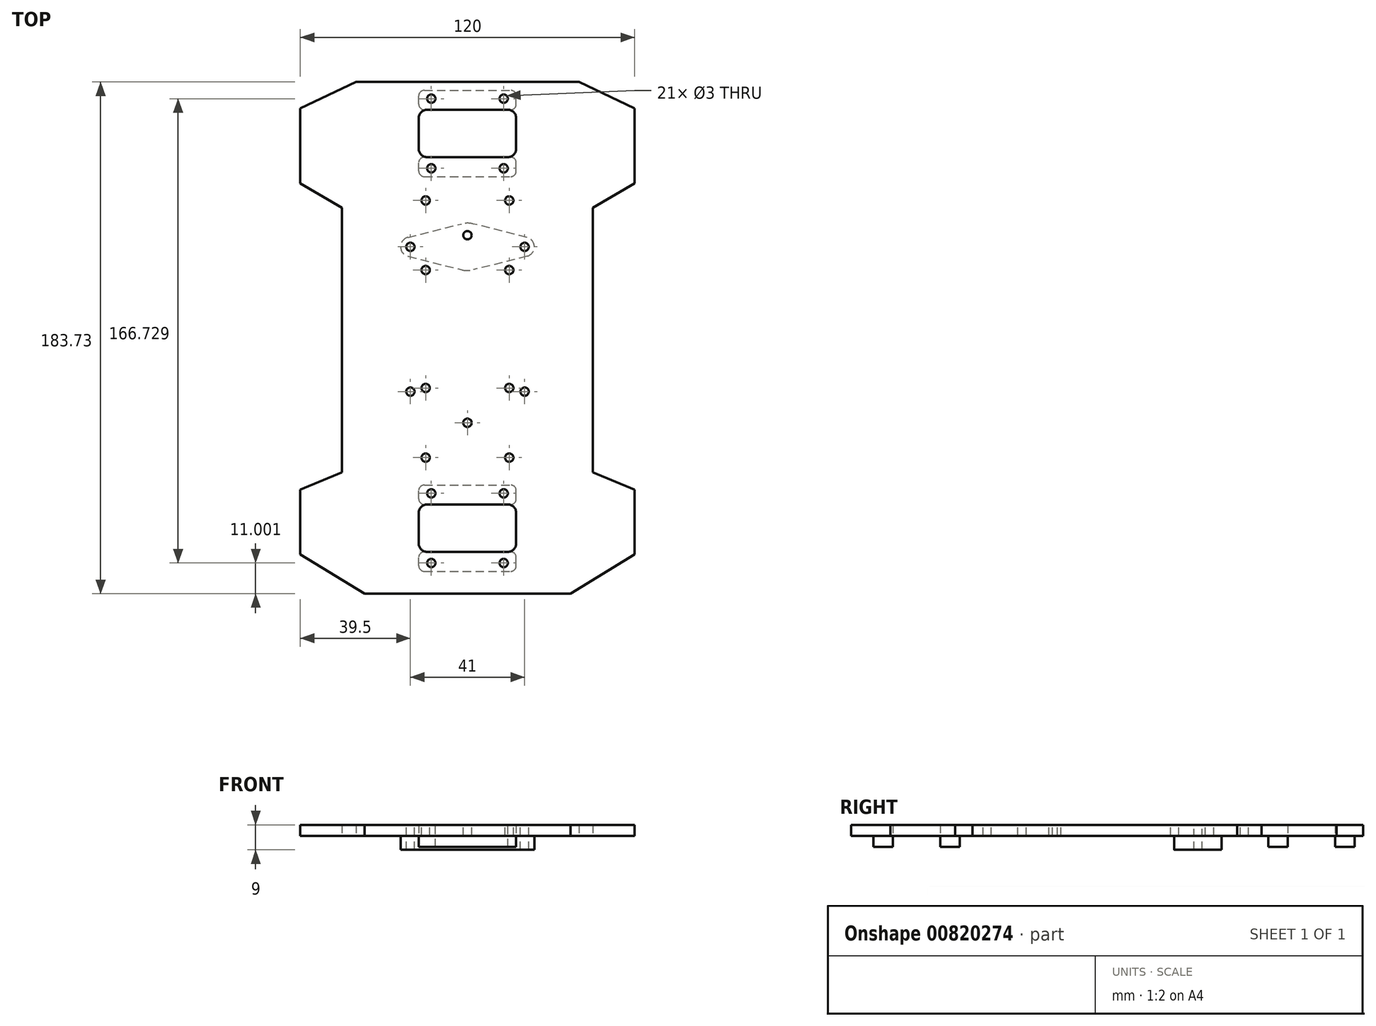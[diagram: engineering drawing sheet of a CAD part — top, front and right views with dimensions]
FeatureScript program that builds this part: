
annotation { "Feature Type Name" : "Feature", "Feature Type Description" : "" }
export const myFeature = defineFeature(function(context is Context, id is Id, definition is map)
    precondition{}
    {
        {
            var Q0;
            Q0=qCreatedBy(makeId("Top.planeOp"),FACE);
            var sketch = newSketch(context, id + "F0", { "sketchPlane" : qUnion([Q0])});
            skLineSegment(sketch, "E0", {"start": v(0, 189.63) * mm, "end": v(0, -203.58) * mm, "construction": true});
            skLineSegment(sketch, "E1", {"start": v(0, 107.51) * mm, "end": v(-40, 107.51) * mm});
            skLineSegment(sketch, "E2", {"start": v(-40, 107.51) * mm, "end": v(-60, 98) * mm});
            skLineSegment(sketch, "E3", {"start": v(-60, 98) * mm, "end": v(-60, 71.1) * mm});
            skLineSegment(sketch, "E4", {"start": v(-60, 71.1) * mm, "end": v(-45, 62.3) * mm});
            skLineSegment(sketch, "E5", {"start": v(-45, 62.3) * mm, "end": v(-45, -32.7) * mm});
            skLineSegment(sketch, "E6", {"start": v(-45, -32.7) * mm, "end": v(-60, -38.9) * mm});
            skLineSegment(sketch, "E7", {"start": v(-60, -38.9) * mm, "end": v(-60, -62.07) * mm});
            skLineSegment(sketch, "E8", {"start": v(-60, -62.07) * mm, "end": v(-36.95, -76.22) * mm});
            skLineSegment(sketch, "E9", {"start": v(-36.95, -76.22) * mm, "end": v(0, -76.22) * mm});
            skLineSegment(sketch, "E10.MirrorCS", {"start": v(45, -32.7) * mm, "end": v(60, -38.9) * mm});
            skLineSegment(sketch, "E11.MirrorCS", {"start": v(40, 107.51) * mm, "end": v(60, 98) * mm});
            skLineSegment(sketch, "E12.MirrorCS", {"start": v(60, -38.9) * mm, "end": v(60, -62.07) * mm});
            skLineSegment(sketch, "E13.MirrorCS", {"start": v(45, 62.3) * mm, "end": v(45, -32.7) * mm});
            skLineSegment(sketch, "E14.MirrorCS", {"start": v(60, -62.07) * mm, "end": v(36.95, -76.22) * mm});
            skLineSegment(sketch, "E15.MirrorCS", {"start": v(60, 71.1) * mm, "end": v(45, 62.3) * mm});
            skLineSegment(sketch, "E16.MirrorCS", {"start": v(60, 98) * mm, "end": v(60, 71.1) * mm});
            skLineSegment(sketch, "E17.MirrorCS", {"start": v(36.95, -76.22) * mm, "end": v(0, -76.22) * mm});
            skLineSegment(sketch, "E18.MirrorCS", {"start": v(0, 107.51) * mm, "end": v(40, 107.51) * mm});
            skLineSegment(sketch, "E19", {"start": v(0, -44.22) * mm, "end": v(-14.5, -44.22) * mm});
            skLineSegment(sketch, "E20", {"start": v(-17.5, -47.22) * mm, "end": v(-17.5, -58.22) * mm});
            skLineSegment(sketch, "E21", {"start": v(-14.5, -61.22) * mm, "end": v(0, -61.22) * mm});
            skLineSegment(sketch, "E22.MirrorCS", {"start": v(14.5, -61.22) * mm, "end": v(0, -61.22) * mm});
            skLineSegment(sketch, "E23.MirrorCS", {"start": v(0, -44.22) * mm, "end": v(14.5, -44.22) * mm});
            skLineSegment(sketch, "E24.MirrorCS", {"start": v(17.5, -47.22) * mm, "end": v(17.5, -58.22) * mm});
            skPoint(sketch, "E25.visualSharp", {"position": v(-17.5, -44.22) * mm});
            skArc(sketch, "E25.filletArc", {"start": v(-14.5, -44.22) * mm, "mid": v(-16.62, -45.1) * mm, "end": v(-17.5, -47.22) * mm});
            skPoint(sketch, "E26.visualSharp", {"position": v(17.5, -44.22) * mm});
            skArc(sketch, "E26.filletArc", {"start": v(17.5, -47.22) * mm, "mid": v(16.62, -45.1) * mm, "end": v(14.5, -44.22) * mm});
            skPoint(sketch, "E27.visualSharp", {"position": v(17.5, -61.22) * mm});
            skArc(sketch, "E27.filletArc", {"start": v(14.5, -61.22) * mm, "mid": v(16.62, -60.34) * mm, "end": v(17.5, -58.22) * mm});
            skPoint(sketch, "E28.visualSharp", {"position": v(-17.5, -61.22) * mm});
            skArc(sketch, "E28.filletArc", {"start": v(-17.5, -58.22) * mm, "mid": v(-16.62, -60.34) * mm, "end": v(-14.5, -61.22) * mm});
            skLineSegment(sketch, "E29", {"start": v(0, 97.51) * mm, "end": v(-14.5, 97.51) * mm});
            skLineSegment(sketch, "E30", {"start": v(-17.5, 94.51) * mm, "end": v(-17.5, 83.51) * mm});
            skLineSegment(sketch, "E31", {"start": v(-14.5, 80.51) * mm, "end": v(0, 80.51) * mm});
            skLineSegment(sketch, "E32.MirrorCS", {"start": v(14.5, 80.51) * mm, "end": v(0, 80.51) * mm});
            skLineSegment(sketch, "E33.MirrorCS", {"start": v(0, 97.51) * mm, "end": v(14.5, 97.51) * mm});
            skLineSegment(sketch, "E34.MirrorCS", {"start": v(17.5, 94.51) * mm, "end": v(17.5, 83.51) * mm});
            skPoint(sketch, "E35.visualSharp", {"position": v(-17.5, 97.51) * mm});
            skArc(sketch, "E35.filletArc", {"start": v(-14.5, 97.51) * mm, "mid": v(-16.62, 96.63) * mm, "end": v(-17.5, 94.51) * mm});
            skPoint(sketch, "E36.visualSharp", {"position": v(17.5, 97.51) * mm});
            skArc(sketch, "E36.filletArc", {"start": v(17.5, 94.51) * mm, "mid": v(16.62, 96.63) * mm, "end": v(14.5, 97.51) * mm});
            skPoint(sketch, "E37.visualSharp", {"position": v(17.5, 80.51) * mm});
            skArc(sketch, "E37.filletArc", {"start": v(14.5, 80.51) * mm, "mid": v(16.62, 81.39) * mm, "end": v(17.5, 83.51) * mm});
            skPoint(sketch, "E38.visualSharp", {"position": v(-17.5, 80.51) * mm});
            skArc(sketch, "E38.filletArc", {"start": v(-17.5, 83.51) * mm, "mid": v(-16.62, 81.39) * mm, "end": v(-14.5, 80.51) * mm});
            skSolve(sketch);
        }
        {
            var Q0;
            Q0=makeQuery(id+"F0.imprint","IMPRINT",FACE,{"disambiguationData":[TD([[makeQuery(id+"F0.imprint","IMPRINT",EDGE,{"derivedFrom":sQuery(id+"F0.wireOp",EDGE,"E1")}),1.0]])]});
            extrude(context, id + "F1", {"entities" : qUnion([Q0]), "depth" : 4 * mm, "offsetDistance" : 25 * mm});
        }
        {
            var Q0;
            Q0=makeQuery(id+"F1.opExtrude","CAP_FACE",FACE,{"disambiguationData":[OSD([sQuery(id+"F0.wireOp",EDGE,"E1"),sQuery(id+"F0.wireOp",EDGE,"E2"),sQuery(id+"F0.wireOp",EDGE,"E3"),sQuery(id+"F0.wireOp",EDGE,"E4"),sQuery(id+"F0.wireOp",EDGE,"E5"),sQuery(id+"F0.wireOp",EDGE,"E6"),sQuery(id+"F0.wireOp",EDGE,"E7"),sQuery(id+"F0.wireOp",EDGE,"E8"),sQuery(id+"F0.wireOp",EDGE,"E9"),sQuery(id+"F0.wireOp",EDGE,"E10.MirrorCS"),sQuery(id+"F0.wireOp",EDGE,"E11.MirrorCS"),sQuery(id+"F0.wireOp",EDGE,"E12.MirrorCS"),sQuery(id+"F0.wireOp",EDGE,"E13.MirrorCS"),sQuery(id+"F0.wireOp",EDGE,"E14.MirrorCS"),sQuery(id+"F0.wireOp",EDGE,"E15.MirrorCS"),sQuery(id+"F0.wireOp",EDGE,"E16.MirrorCS"),sQuery(id+"F0.wireOp",EDGE,"E17.MirrorCS"),sQuery(id+"F0.wireOp",EDGE,"E18.MirrorCS"),sQuery(id+"F0.wireOp",EDGE,"E19"),sQuery(id+"F0.wireOp",EDGE,"E20"),sQuery(id+"F0.wireOp",EDGE,"E21"),sQuery(id+"F0.wireOp",EDGE,"E22.MirrorCS"),sQuery(id+"F0.wireOp",EDGE,"E23.MirrorCS"),sQuery(id+"F0.wireOp",EDGE,"E24.MirrorCS"),sQuery(id+"F0.wireOp",EDGE,"E25.filletArc"),sQuery(id+"F0.wireOp",EDGE,"E26.filletArc"),sQuery(id+"F0.wireOp",EDGE,"E27.filletArc"),sQuery(id+"F0.wireOp",EDGE,"E28.filletArc"),sQuery(id+"F0.wireOp",EDGE,"E29"),sQuery(id+"F0.wireOp",EDGE,"E30"),sQuery(id+"F0.wireOp",EDGE,"E31"),sQuery(id+"F0.wireOp",EDGE,"E32.MirrorCS"),sQuery(id+"F0.wireOp",EDGE,"E33.MirrorCS"),sQuery(id+"F0.wireOp",EDGE,"E34.MirrorCS"),sQuery(id+"F0.wireOp",EDGE,"E35.filletArc"),sQuery(id+"F0.wireOp",EDGE,"E36.filletArc"),sQuery(id+"F0.wireOp",EDGE,"E37.filletArc"),sQuery(id+"F0.wireOp",EDGE,"E38.filletArc")])],"isStart":true});
            var sketch = newSketch(context, id + "F2", { "sketchPlane" : qUnion([Q0])});
            skLineSegment(sketch, "E39.bottom", {"start": v(-15.5, 68.22) * mm, "end": v(15.5, 68.22) * mm});
            skLineSegment(sketch, "E39.top", {"start": v(-15.5, 61.22) * mm, "end": v(15.5, 61.22) * mm});
            skLineSegment(sketch, "E39.left", {"start": v(-17.5, 66.22) * mm, "end": v(-17.5, 63.22) * mm});
            skLineSegment(sketch, "E39.right", {"start": v(17.5, 66.22) * mm, "end": v(17.5, 63.22) * mm});
            skLineSegment(sketch, "E40.bottom", {"start": v(-15.5, 44.22) * mm, "end": v(15.5, 44.22) * mm});
            skLineSegment(sketch, "E40.top", {"start": v(-15.5, 37.22) * mm, "end": v(15.5, 37.22) * mm});
            skLineSegment(sketch, "E40.left", {"start": v(-17.5, 42.22) * mm, "end": v(-17.5, 39.22) * mm});
            skLineSegment(sketch, "E40.right", {"start": v(17.5, 42.22) * mm, "end": v(17.5, 39.22) * mm});
            skLineSegment(sketch, "E41.bottom", {"start": v(-15.5, -73.51) * mm, "end": v(15.5, -73.51) * mm});
            skLineSegment(sketch, "E41.top", {"start": v(-15.5, -80.51) * mm, "end": v(15.5, -80.51) * mm});
            skLineSegment(sketch, "E41.left", {"start": v(-17.5, -75.51) * mm, "end": v(-17.5, -78.51) * mm});
            skLineSegment(sketch, "E41.right", {"start": v(17.5, -75.51) * mm, "end": v(17.5, -78.51) * mm});
            skLineSegment(sketch, "E42.bottom", {"start": v(-15.5, -97.51) * mm, "end": v(15.5, -97.51) * mm});
            skLineSegment(sketch, "E42.top", {"start": v(-15.5, -104.51) * mm, "end": v(15.5, -104.51) * mm});
            skLineSegment(sketch, "E42.left", {"start": v(-17.5, -99.51) * mm, "end": v(-17.5, -102.51) * mm});
            skLineSegment(sketch, "E42.right", {"start": v(17.5, -99.51) * mm, "end": v(17.5, -102.51) * mm});
            skPoint(sketch, "E43.visualSharp", {"position": v(-17.5, -73.51) * mm});
            skArc(sketch, "E43.filletArc", {"start": v(-15.5, -73.51) * mm, "mid": v(-16.91, -74.1) * mm, "end": v(-17.5, -75.51) * mm});
            skPoint(sketch, "E44.visualSharp", {"position": v(-17.5, -80.51) * mm});
            skArc(sketch, "E44.filletArc", {"start": v(-17.5, -78.51) * mm, "mid": v(-16.91, -79.92) * mm, "end": v(-15.5, -80.51) * mm});
            skPoint(sketch, "E45.visualSharp", {"position": v(17.5, -80.51) * mm});
            skArc(sketch, "E45.filletArc", {"start": v(15.5, -80.51) * mm, "mid": v(16.91, -79.92) * mm, "end": v(17.5, -78.51) * mm});
            skPoint(sketch, "E46.visualSharp", {"position": v(17.5, -73.51) * mm});
            skArc(sketch, "E46.filletArc", {"start": v(17.5, -75.51) * mm, "mid": v(16.91, -74.1) * mm, "end": v(15.5, -73.51) * mm});
            skPoint(sketch, "E47.visualSharp", {"position": v(17.5, -97.51) * mm});
            skArc(sketch, "E47.filletArc", {"start": v(17.5, -99.51) * mm, "mid": v(16.91, -98.1) * mm, "end": v(15.5, -97.51) * mm});
            skPoint(sketch, "E48.visualSharp", {"position": v(17.5, -104.51) * mm});
            skArc(sketch, "E48.filletArc", {"start": v(15.5, -104.51) * mm, "mid": v(16.91, -103.92) * mm, "end": v(17.5, -102.51) * mm});
            skPoint(sketch, "E49.visualSharp", {"position": v(-17.5, -104.51) * mm});
            skArc(sketch, "E49.filletArc", {"start": v(-17.5, -102.51) * mm, "mid": v(-16.91, -103.92) * mm, "end": v(-15.5, -104.51) * mm});
            skPoint(sketch, "E50.visualSharp", {"position": v(-17.5, -97.51) * mm});
            skArc(sketch, "E50.filletArc", {"start": v(-15.5, -97.51) * mm, "mid": v(-16.91, -98.1) * mm, "end": v(-17.5, -99.51) * mm});
            skPoint(sketch, "E51.visualSharp", {"position": v(-17.5, 37.22) * mm});
            skArc(sketch, "E51.filletArc", {"start": v(-17.5, 39.22) * mm, "mid": v(-16.91, 37.8) * mm, "end": v(-15.5, 37.22) * mm});
            skPoint(sketch, "E52.visualSharp", {"position": v(-17.5, 44.22) * mm});
            skArc(sketch, "E52.filletArc", {"start": v(-15.5, 44.22) * mm, "mid": v(-16.91, 43.63) * mm, "end": v(-17.5, 42.22) * mm});
            skPoint(sketch, "E53.visualSharp", {"position": v(17.5, 37.22) * mm});
            skArc(sketch, "E53.filletArc", {"start": v(15.5, 37.22) * mm, "mid": v(16.91, 37.8) * mm, "end": v(17.5, 39.22) * mm});
            skPoint(sketch, "E54.visualSharp", {"position": v(17.5, 61.22) * mm});
            skArc(sketch, "E54.filletArc", {"start": v(15.5, 61.22) * mm, "mid": v(16.91, 61.8) * mm, "end": v(17.5, 63.22) * mm});
            skPoint(sketch, "E55.visualSharp", {"position": v(17.5, 68.22) * mm});
            skArc(sketch, "E55.filletArc", {"start": v(17.5, 66.22) * mm, "mid": v(16.91, 67.63) * mm, "end": v(15.5, 68.22) * mm});
            skPoint(sketch, "E56.visualSharp", {"position": v(-17.5, 68.22) * mm});
            skArc(sketch, "E56.filletArc", {"start": v(-15.5, 68.22) * mm, "mid": v(-16.91, 67.63) * mm, "end": v(-17.5, 66.22) * mm});
            skPoint(sketch, "E57.visualSharp", {"position": v(-17.5, 61.22) * mm});
            skArc(sketch, "E57.filletArc", {"start": v(-17.5, 63.22) * mm, "mid": v(-16.91, 61.8) * mm, "end": v(-15.5, 61.22) * mm});
            skPoint(sketch, "E58.visualSharp", {"position": v(17.5, 44.22) * mm});
            skArc(sketch, "E58.filletArc", {"start": v(17.5, 42.22) * mm, "mid": v(16.91, 43.63) * mm, "end": v(15.5, 44.22) * mm});
            skSolve(sketch);
        }
        {
            var Q0;
            Q0 = qSketchRegion(id + "F2", true);
            extrude(context, id + "F3", {"entities" : qUnion([Q0]), "operationType" : NewBodyOperationType.ADD, "depth" : 4 * mm, "offsetDistance" : 25 * mm});
        }
        {
            var Q0;
            Q0=makeQuery(id+"F1.opExtrude","CAP_FACE",FACE,{"disambiguationData":[OSD([sQuery(id+"F0.wireOp",EDGE,"E1"),sQuery(id+"F0.wireOp",EDGE,"E2"),sQuery(id+"F0.wireOp",EDGE,"E3"),sQuery(id+"F0.wireOp",EDGE,"E4"),sQuery(id+"F0.wireOp",EDGE,"E5"),sQuery(id+"F0.wireOp",EDGE,"E6"),sQuery(id+"F0.wireOp",EDGE,"E7"),sQuery(id+"F0.wireOp",EDGE,"E8"),sQuery(id+"F0.wireOp",EDGE,"E9"),sQuery(id+"F0.wireOp",EDGE,"E10.MirrorCS"),sQuery(id+"F0.wireOp",EDGE,"E11.MirrorCS"),sQuery(id+"F0.wireOp",EDGE,"E12.MirrorCS"),sQuery(id+"F0.wireOp",EDGE,"E13.MirrorCS"),sQuery(id+"F0.wireOp",EDGE,"E14.MirrorCS"),sQuery(id+"F0.wireOp",EDGE,"E15.MirrorCS"),sQuery(id+"F0.wireOp",EDGE,"E16.MirrorCS"),sQuery(id+"F0.wireOp",EDGE,"E17.MirrorCS"),sQuery(id+"F0.wireOp",EDGE,"E18.MirrorCS"),sQuery(id+"F0.wireOp",EDGE,"E19"),sQuery(id+"F0.wireOp",EDGE,"E20"),sQuery(id+"F0.wireOp",EDGE,"E21"),sQuery(id+"F0.wireOp",EDGE,"E22.MirrorCS"),sQuery(id+"F0.wireOp",EDGE,"E23.MirrorCS"),sQuery(id+"F0.wireOp",EDGE,"E24.MirrorCS"),sQuery(id+"F0.wireOp",EDGE,"E25.filletArc"),sQuery(id+"F0.wireOp",EDGE,"E26.filletArc"),sQuery(id+"F0.wireOp",EDGE,"E27.filletArc"),sQuery(id+"F0.wireOp",EDGE,"E28.filletArc"),sQuery(id+"F0.wireOp",EDGE,"E29"),sQuery(id+"F0.wireOp",EDGE,"E30"),sQuery(id+"F0.wireOp",EDGE,"E31"),sQuery(id+"F0.wireOp",EDGE,"E32.MirrorCS"),sQuery(id+"F0.wireOp",EDGE,"E33.MirrorCS"),sQuery(id+"F0.wireOp",EDGE,"E34.MirrorCS"),sQuery(id+"F0.wireOp",EDGE,"E35.filletArc"),sQuery(id+"F0.wireOp",EDGE,"E36.filletArc"),sQuery(id+"F0.wireOp",EDGE,"E37.filletArc"),sQuery(id+"F0.wireOp",EDGE,"E38.filletArc")])],"isStart":false});
            var sketch = newSketch(context, id + "F4", { "sketchPlane" : qUnion([Q0])});
            skCircle(sketch, "E59", {"center": v(-20.5, 48.3) * mm, "radius": 1.5 * mm});
            skCircle(sketch, "E60.0.1.0", {"center": v(-20.5, -3.7) * mm, "radius": 1.5 * mm});
            skCircle(sketch, "E60.1.0.0", {"center": v(20.5, 48.3) * mm, "radius": 1.5 * mm});
            skCircle(sketch, "E60.1.1.0", {"center": v(20.5, -3.7) * mm, "radius": 1.5 * mm});
            skLineSegment(sketch, "E60.direction1", {"start": v(-20.5, 48.3) * mm, "end": v(20.5, 48.3) * mm, "construction": true});
            skLineSegment(sketch, "E60.direction2", {"start": v(-20.5, 48.3) * mm, "end": v(-20.5, -3.7) * mm, "construction": true});
            skLineSegment(sketch, "E61", {"start": v(0, 70.67) * mm, "end": v(0, -11.9) * mm, "construction": true});
            skLineSegment(sketch, "E62", {"start": v(-45, 62.3) * mm, "end": v(45, 62.3) * mm, "construction": true});
            skSolve(sketch);
        }
        {
            var Q0;
            Q0 = qSketchRegion(id + "F4", true);
            extrude(context, id + "F5", {"entities" : qUnion([Q0]), "operationType" : NewBodyOperationType.REMOVE, "oppositeDirection" : true, "depth" : 25 * mm, "offsetDistance" : 25 * mm});
        }
        {
            var Q0;
            Q0=makeQuery(id+"F1.opExtrude","CAP_FACE",FACE,{"disambiguationData":[OSD([sQuery(id+"F0.wireOp",EDGE,"E1"),sQuery(id+"F0.wireOp",EDGE,"E2"),sQuery(id+"F0.wireOp",EDGE,"E3"),sQuery(id+"F0.wireOp",EDGE,"E4"),sQuery(id+"F0.wireOp",EDGE,"E5"),sQuery(id+"F0.wireOp",EDGE,"E6"),sQuery(id+"F0.wireOp",EDGE,"E7"),sQuery(id+"F0.wireOp",EDGE,"E8"),sQuery(id+"F0.wireOp",EDGE,"E9"),sQuery(id+"F0.wireOp",EDGE,"E10.MirrorCS"),sQuery(id+"F0.wireOp",EDGE,"E11.MirrorCS"),sQuery(id+"F0.wireOp",EDGE,"E12.MirrorCS"),sQuery(id+"F0.wireOp",EDGE,"E13.MirrorCS"),sQuery(id+"F0.wireOp",EDGE,"E14.MirrorCS"),sQuery(id+"F0.wireOp",EDGE,"E15.MirrorCS"),sQuery(id+"F0.wireOp",EDGE,"E16.MirrorCS"),sQuery(id+"F0.wireOp",EDGE,"E17.MirrorCS"),sQuery(id+"F0.wireOp",EDGE,"E18.MirrorCS"),sQuery(id+"F0.wireOp",EDGE,"E19"),sQuery(id+"F0.wireOp",EDGE,"E20"),sQuery(id+"F0.wireOp",EDGE,"E21"),sQuery(id+"F0.wireOp",EDGE,"E22.MirrorCS"),sQuery(id+"F0.wireOp",EDGE,"E23.MirrorCS"),sQuery(id+"F0.wireOp",EDGE,"E24.MirrorCS"),sQuery(id+"F0.wireOp",EDGE,"E25.filletArc"),sQuery(id+"F0.wireOp",EDGE,"E26.filletArc"),sQuery(id+"F0.wireOp",EDGE,"E27.filletArc"),sQuery(id+"F0.wireOp",EDGE,"E28.filletArc"),sQuery(id+"F0.wireOp",EDGE,"E29"),sQuery(id+"F0.wireOp",EDGE,"E30"),sQuery(id+"F0.wireOp",EDGE,"E31"),sQuery(id+"F0.wireOp",EDGE,"E32.MirrorCS"),sQuery(id+"F0.wireOp",EDGE,"E33.MirrorCS"),sQuery(id+"F0.wireOp",EDGE,"E34.MirrorCS"),sQuery(id+"F0.wireOp",EDGE,"E35.filletArc"),sQuery(id+"F0.wireOp",EDGE,"E36.filletArc"),sQuery(id+"F0.wireOp",EDGE,"E37.filletArc"),sQuery(id+"F0.wireOp",EDGE,"E38.filletArc")])],"isStart":false});
            var sketch = newSketch(context, id + "F6", { "sketchPlane" : qUnion([Q0])});
            skCircle(sketch, "E63", {"center": v(-13, -40.22) * mm, "radius": 1.5 * mm});
            skCircle(sketch, "E64.0.1.0", {"center": v(-13, -65.22) * mm, "radius": 1.5 * mm});
            skCircle(sketch, "E64.1.0.0", {"center": v(13, -40.22) * mm, "radius": 1.5 * mm});
            skCircle(sketch, "E64.1.1.0", {"center": v(13, -65.22) * mm, "radius": 1.5 * mm});
            skLineSegment(sketch, "E64.direction1", {"start": v(-13, -40.22) * mm, "end": v(13, -40.22) * mm, "construction": true});
            skLineSegment(sketch, "E64.direction2", {"start": v(-13, -40.22) * mm, "end": v(-13, -65.22) * mm, "construction": true});
            skLineSegment(sketch, "E65", {"start": v(13, -65.22) * mm, "end": v(-13, -65.22) * mm, "construction": true});
            skLineSegment(sketch, "E66", {"start": v(-17.5, -52.72) * mm, "end": v(17.5, -52.72) * mm, "construction": true});
            skLineSegment(sketch, "E67", {"start": v(0, -44.22) * mm, "end": v(0, -61.22) * mm, "construction": true});
            skCircle(sketch, "E68", {"center": v(-13, 101.51) * mm, "radius": 1.5 * mm});
            skCircle(sketch, "E69.0.1.0", {"center": v(-13, 76.51) * mm, "radius": 1.5 * mm});
            skCircle(sketch, "E69.1.0.0", {"center": v(13, 101.51) * mm, "radius": 1.5 * mm});
            skCircle(sketch, "E69.1.1.0", {"center": v(13, 76.51) * mm, "radius": 1.5 * mm});
            skLineSegment(sketch, "E69.direction1", {"start": v(-13, 101.51) * mm, "end": v(13, 101.51) * mm, "construction": true});
            skLineSegment(sketch, "E69.direction2", {"start": v(-13, 101.51) * mm, "end": v(-13, 76.51) * mm, "construction": true});
            skLineSegment(sketch, "E70", {"start": v(13, 76.51) * mm, "end": v(-13, 76.51) * mm, "construction": true});
            skLineSegment(sketch, "E71", {"start": v(0, 106.76) * mm, "end": v(0, 57.44) * mm, "construction": true});
            skLineSegment(sketch, "E72", {"start": v(-17.5, 89.01) * mm, "end": v(17.5, 89.01) * mm, "construction": true});
            skSolve(sketch);
        }
        {
            var Q0;
            Q0 = qSketchRegion(id + "F6", true);
            extrude(context, id + "F7", {"entities" : qUnion([Q0]), "operationType" : NewBodyOperationType.REMOVE, "oppositeDirection" : true, "depth" : 25 * mm, "offsetDistance" : 25 * mm});
        }
        {
            var Q0;
            Q0=makeQuery(id+"F1.opExtrude","CAP_FACE",FACE,{"disambiguationData":[OSD([sQuery(id+"F0.wireOp",EDGE,"E1"),sQuery(id+"F0.wireOp",EDGE,"E2"),sQuery(id+"F0.wireOp",EDGE,"E3"),sQuery(id+"F0.wireOp",EDGE,"E4"),sQuery(id+"F0.wireOp",EDGE,"E5"),sQuery(id+"F0.wireOp",EDGE,"E6"),sQuery(id+"F0.wireOp",EDGE,"E7"),sQuery(id+"F0.wireOp",EDGE,"E8"),sQuery(id+"F0.wireOp",EDGE,"E9"),sQuery(id+"F0.wireOp",EDGE,"E10.MirrorCS"),sQuery(id+"F0.wireOp",EDGE,"E11.MirrorCS"),sQuery(id+"F0.wireOp",EDGE,"E12.MirrorCS"),sQuery(id+"F0.wireOp",EDGE,"E13.MirrorCS"),sQuery(id+"F0.wireOp",EDGE,"E14.MirrorCS"),sQuery(id+"F0.wireOp",EDGE,"E15.MirrorCS"),sQuery(id+"F0.wireOp",EDGE,"E16.MirrorCS"),sQuery(id+"F0.wireOp",EDGE,"E17.MirrorCS"),sQuery(id+"F0.wireOp",EDGE,"E18.MirrorCS"),sQuery(id+"F0.wireOp",EDGE,"E19"),sQuery(id+"F0.wireOp",EDGE,"E20"),sQuery(id+"F0.wireOp",EDGE,"E21"),sQuery(id+"F0.wireOp",EDGE,"E22.MirrorCS"),sQuery(id+"F0.wireOp",EDGE,"E23.MirrorCS"),sQuery(id+"F0.wireOp",EDGE,"E24.MirrorCS"),sQuery(id+"F0.wireOp",EDGE,"E25.filletArc"),sQuery(id+"F0.wireOp",EDGE,"E26.filletArc"),sQuery(id+"F0.wireOp",EDGE,"E27.filletArc"),sQuery(id+"F0.wireOp",EDGE,"E28.filletArc"),sQuery(id+"F0.wireOp",EDGE,"E29"),sQuery(id+"F0.wireOp",EDGE,"E30"),sQuery(id+"F0.wireOp",EDGE,"E31"),sQuery(id+"F0.wireOp",EDGE,"E32.MirrorCS"),sQuery(id+"F0.wireOp",EDGE,"E33.MirrorCS"),sQuery(id+"F0.wireOp",EDGE,"E34.MirrorCS"),sQuery(id+"F0.wireOp",EDGE,"E35.filletArc"),sQuery(id+"F0.wireOp",EDGE,"E36.filletArc"),sQuery(id+"F0.wireOp",EDGE,"E37.filletArc"),sQuery(id+"F0.wireOp",EDGE,"E38.filletArc")])],"isStart":false});
            var sketch = newSketch(context, id + "F8", { "sketchPlane" : qUnion([Q0])});
            skCircle(sketch, "E73", {"center": v(-15, -2.38) * mm, "radius": 1.5 * mm});
            skCircle(sketch, "E74.0.1.0", {"center": v(-15, -27.38) * mm, "radius": 1.5 * mm});
            skCircle(sketch, "E74.1.0.0", {"center": v(15, -2.38) * mm, "radius": 1.5 * mm});
            skCircle(sketch, "E74.1.1.0", {"center": v(15, -27.38) * mm, "radius": 1.5 * mm});
            skLineSegment(sketch, "E74.direction1", {"start": v(-15, -2.38) * mm, "end": v(15, -2.38) * mm, "construction": true});
            skLineSegment(sketch, "E74.direction2", {"start": v(-15, -2.38) * mm, "end": v(-15, -27.38) * mm, "construction": true});
            skLineSegment(sketch, "E75", {"start": v(0, 0) * mm, "end": v(0, -52.65) * mm, "construction": true});
            skCircle(sketch, "E76", {"center": v(-15, 64.97) * mm, "radius": 1.5 * mm});
            skCircle(sketch, "E77.0.1.0", {"center": v(-15, 39.97) * mm, "radius": 1.5 * mm});
            skCircle(sketch, "E77.1.0.0", {"center": v(15, 64.97) * mm, "radius": 1.5 * mm});
            skCircle(sketch, "E77.1.1.0", {"center": v(15, 39.97) * mm, "radius": 1.5 * mm});
            skLineSegment(sketch, "E77.direction1", {"start": v(-15, 64.97) * mm, "end": v(15, 64.97) * mm, "construction": true});
            skLineSegment(sketch, "E77.direction2", {"start": v(-15, 64.97) * mm, "end": v(-15, 39.97) * mm, "construction": true});
            skLineSegment(sketch, "E78", {"start": v(15, -27.38) * mm, "end": v(-15, -2.38) * mm, "construction": true});
            skLineSegment(sketch, "E79", {"start": v(15, -2.38) * mm, "end": v(-15, -27.38) * mm, "construction": true});
            skLineSegment(sketch, "E80", {"start": v(15, 39.97) * mm, "end": v(-15, 64.97) * mm, "construction": true});
            skLineSegment(sketch, "E81", {"start": v(15, 64.97) * mm, "end": v(-15, 39.97) * mm, "construction": true});
            skCircle(sketch, "E82", {"center": v(0, 52.47) * mm, "radius": 1.5 * mm});
            skCircle(sketch, "E83", {"center": v(0, -14.88) * mm, "radius": 1.5 * mm});
            skSolve(sketch);
        }
        {
            var Q0;
            Q0 = qSketchRegion(id + "F8", true);
            extrude(context, id + "F9", {"entities" : qUnion([Q0]), "operationType" : NewBodyOperationType.REMOVE, "oppositeDirection" : true, "depth" : 25 * mm, "offsetDistance" : 25 * mm});
        }
        {
            var Q0;
            Q0=makeQuery(id+"F1.opExtrude","CAP_FACE",FACE,{"disambiguationData":[OSD([sQuery(id+"F0.wireOp",EDGE,"E1"),sQuery(id+"F0.wireOp",EDGE,"E2"),sQuery(id+"F0.wireOp",EDGE,"E3"),sQuery(id+"F0.wireOp",EDGE,"E4"),sQuery(id+"F0.wireOp",EDGE,"E5"),sQuery(id+"F0.wireOp",EDGE,"E6"),sQuery(id+"F0.wireOp",EDGE,"E7"),sQuery(id+"F0.wireOp",EDGE,"E8"),sQuery(id+"F0.wireOp",EDGE,"E9"),sQuery(id+"F0.wireOp",EDGE,"E10.MirrorCS"),sQuery(id+"F0.wireOp",EDGE,"E11.MirrorCS"),sQuery(id+"F0.wireOp",EDGE,"E12.MirrorCS"),sQuery(id+"F0.wireOp",EDGE,"E13.MirrorCS"),sQuery(id+"F0.wireOp",EDGE,"E14.MirrorCS"),sQuery(id+"F0.wireOp",EDGE,"E15.MirrorCS"),sQuery(id+"F0.wireOp",EDGE,"E16.MirrorCS"),sQuery(id+"F0.wireOp",EDGE,"E17.MirrorCS"),sQuery(id+"F0.wireOp",EDGE,"E18.MirrorCS"),sQuery(id+"F0.wireOp",EDGE,"E19"),sQuery(id+"F0.wireOp",EDGE,"E20"),sQuery(id+"F0.wireOp",EDGE,"E21"),sQuery(id+"F0.wireOp",EDGE,"E22.MirrorCS"),sQuery(id+"F0.wireOp",EDGE,"E23.MirrorCS"),sQuery(id+"F0.wireOp",EDGE,"E24.MirrorCS"),sQuery(id+"F0.wireOp",EDGE,"E25.filletArc"),sQuery(id+"F0.wireOp",EDGE,"E26.filletArc"),sQuery(id+"F0.wireOp",EDGE,"E27.filletArc"),sQuery(id+"F0.wireOp",EDGE,"E28.filletArc"),sQuery(id+"F0.wireOp",EDGE,"E29"),sQuery(id+"F0.wireOp",EDGE,"E30"),sQuery(id+"F0.wireOp",EDGE,"E31"),sQuery(id+"F0.wireOp",EDGE,"E32.MirrorCS"),sQuery(id+"F0.wireOp",EDGE,"E33.MirrorCS"),sQuery(id+"F0.wireOp",EDGE,"E34.MirrorCS"),sQuery(id+"F0.wireOp",EDGE,"E35.filletArc"),sQuery(id+"F0.wireOp",EDGE,"E36.filletArc"),sQuery(id+"F0.wireOp",EDGE,"E37.filletArc"),sQuery(id+"F0.wireOp",EDGE,"E38.filletArc")])],"isStart":true});
            var sketch = newSketch(context, id + "F10", { "sketchPlane" : qUnion([Q0])});
            skLineSegment(sketch, "E84", {"start": v(20.5, -48.3) * mm, "end": v(-20.5, -48.3) * mm, "construction": true});
            skArc(sketch, "E85", {"start": v(2.07, -40.06) * mm, "mid": v(0, -39.8) * mm, "end": v(-2.07, -40.06) * mm});
            skCircle(sketch, "E86", {"center": v(20.5, -48.3) * mm, "radius": 3.5 * mm});
            skCircle(sketch, "E87", {"center": v(-20.5, -48.3) * mm, "radius": 3.5 * mm});
            skLineSegment(sketch, "E88", {"start": v(21.35, -51.7) * mm, "end": v(2.07, -56.55) * mm});
            skLineSegment(sketch, "E89", {"start": v(21.35, -44.91) * mm, "end": v(2.07, -40.06) * mm});
            skLineSegment(sketch, "E90", {"start": v(-21.35, -44.91) * mm, "end": v(-2.07, -40.06) * mm});
            skLineSegment(sketch, "E91", {"start": v(-21.35, -51.7) * mm, "end": v(-2.07, -56.55) * mm});
            skArc(sketch, "E92.trimOffspring", {"start": v(-2.07, -56.55) * mm, "mid": v(0, -56.8) * mm, "end": v(2.07, -56.55) * mm});
            skCircle(sketch, "E93.0", {"center": v(20.5, -48.3) * mm, "radius": 1.5 * mm});
            skCircle(sketch, "E94.0", {"center": v(-20.5, -48.3) * mm, "radius": 1.5 * mm});
            skSolve(sketch);
        }
        {
            var Q0;
            Q0 = qSketchRegion(id + "F10", true);
            extrude(context, id + "F11", {"entities" : qUnion([Q0]), "operationType" : NewBodyOperationType.ADD, "depth" : 5 * mm, "offsetDistance" : 25 * mm});
        }
    });
